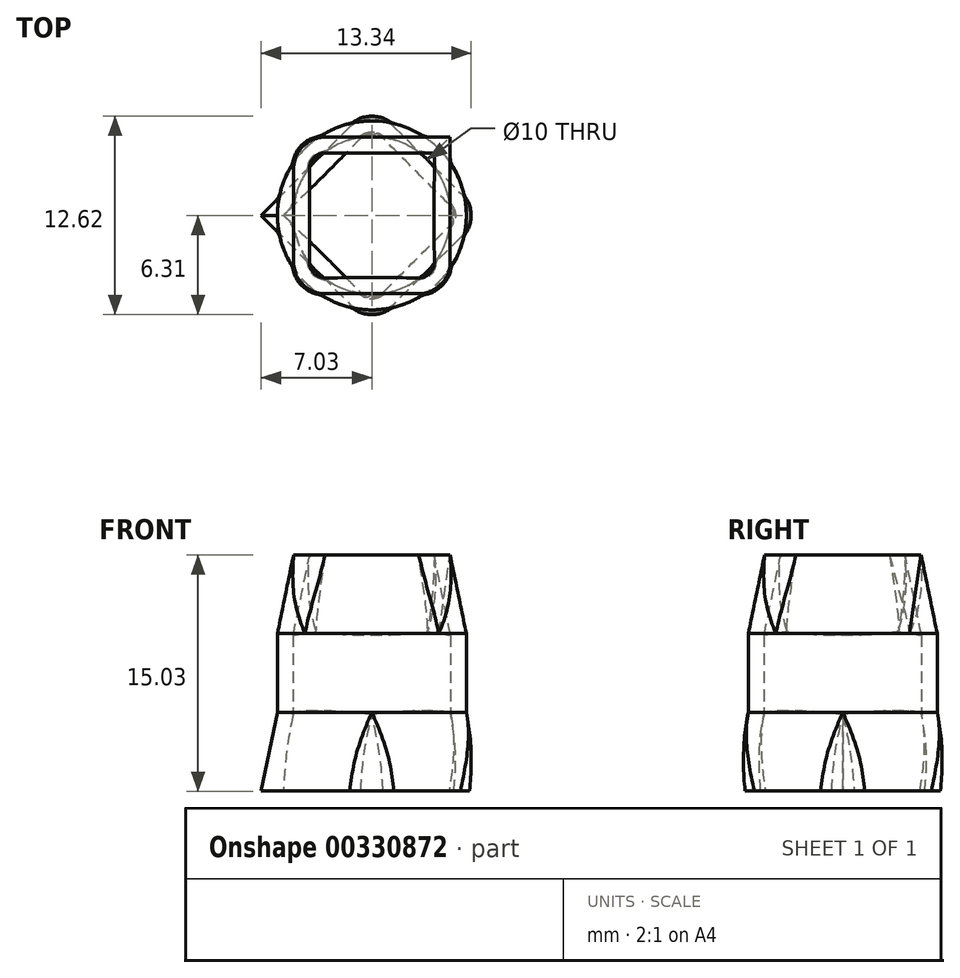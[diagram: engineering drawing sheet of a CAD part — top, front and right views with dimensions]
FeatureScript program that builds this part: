
annotation { "Feature Type Name" : "Feature", "Feature Type Description" : "" }
export const myFeature = defineFeature(function(context is Context, id is Id, definition is map)
    precondition{}
    {
        {
            var Q0;
            Q0=qCreatedBy(makeId("Top.planeOp"),FACE);
            var sketch = newSketch(context, id + "F0", { "sketchPlane" : qUnion([Q0])});
            skCircle(sketch, "E0", {"center": v(0, 0) * mm, "radius": 6 * mm});
            skSolve(sketch);
        }
        {
            var Q0;
            Q0=makeQuery(id+"F0.imprint","IMPRINT",FACE,{"disambiguationData":[TD([[makeQuery(id+"F0.imprint","IMPRINT",EDGE,{"derivedFrom":sQuery(id+"F0.wireOp",EDGE,"E0")}),1.0]])]});
            extrude(context, id + "F1", {"entities" : qUnion([Q0]), "endBound" : BoundingType.SYMMETRIC, "depth" : 5 * mm});
        }
        {
            var Q0;
            Q0=makeQuery(id+"F1.opExtrude","CAP_FACE",FACE,{"disambiguationData":[OSD([sQuery(id+"F0.wireOp",EDGE,"E0")])],"isStart":false});
            cPlane(context, id + "F2", {"entities" : qUnion([Q0]), "cplaneType" : CPlaneType.OFFSET, "offset" : 5 * mm, "width" : 150 * mm, "height" : 150 * mm});
        }
        {
            var Q0;
            Q0=qCreatedBy(id+"F2.planeOp",FACE);
            var sketch = newSketch(context, id + "F3", { "sketchPlane" : qUnion([Q0])});
            skLineSegment(sketch, "E1.bottom", {"start": v(4.97, -4.97) * mm, "end": v(-4.97, -4.97) * mm});
            skLineSegment(sketch, "E1.top", {"start": v(4.97, 4.97) * mm, "end": v(-4.97, 4.97) * mm});
            skLineSegment(sketch, "E1.left", {"start": v(4.97, -4.97) * mm, "end": v(4.97, 4.97) * mm});
            skLineSegment(sketch, "E1.right", {"start": v(-4.97, -4.97) * mm, "end": v(-4.97, 4.97) * mm});
            skPoint(sketch, "E1.middle", {"position": v(0, 0) * mm});
            skLineSegment(sketch, "E2", {"start": v(4.97, 0) * mm, "end": v(6, 0) * mm, "construction": true});
            skPoint(sketch, "E2.endSnap0", {"position": v(4.97, 0) * mm});
            skLineSegment(sketch, "E3", {"start": v(4.97, -4.97) * mm, "end": v(4.24, -4.24) * mm, "construction": true});
            skSolve(sketch);
        }
        {
            var Q0;
            Q0=makeQuery(id+"F1.opExtrude","CAP_FACE",FACE,{"disambiguationData":[OSD([sQuery(id+"F0.wireOp",EDGE,"E0")])],"isStart":false});
            var Q1;
            Q1=makeQuery(id+"F3.imprint","IMPRINT",FACE,{"disambiguationData":[TD([[makeQuery(id+"F3.imprint","IMPRINT",EDGE,{"derivedFrom":sQuery(id+"F3.wireOp",EDGE,"E1.bottom")}),-1.0]])]});
            loft(context, id + "F4", {"operationType" : NewBodyOperationType.ADD, "sheetProfilesArray" : [{ "sheetProfileEntities" : qUnion([Q0]) }, { "sheetProfileEntities" : qUnion([Q1]) }]});
        }
        {
            var Q0;
            Q0=makeQuery(id+"F1.opExtrude","CAP_FACE",FACE,{"disambiguationData":[OSD([sQuery(id+"F0.wireOp",EDGE,"E0")])],"isStart":true});
            cPlane(context, id + "F5", {"entities" : qUnion([Q0]), "cplaneType" : CPlaneType.OFFSET, "offset" : 5 * mm, "width" : 150 * mm, "height" : 150 * mm});
        }
        {
            var Q0;
            Q0=qCreatedBy(id+"F5.planeOp",FACE);
            var sketch = newSketch(context, id + "F6", { "sketchPlane" : qUnion([Q0])});
            skLineSegment(sketch, "E4.bottom", {"start": v(0, -7.03) * mm, "end": v(7.03, 0) * mm});
            skLineSegment(sketch, "E4.top", {"start": v(-7.03, 0) * mm, "end": v(0, 7.03) * mm});
            skLineSegment(sketch, "E4.left", {"start": v(0, -7.03) * mm, "end": v(-7.03, 0) * mm});
            skLineSegment(sketch, "E4.right", {"start": v(7.03, 0) * mm, "end": v(0, 7.03) * mm});
            skPoint(sketch, "E4.middle", {"position": v(0, 0) * mm});
            skSolve(sketch);
        }
        {
            var Q0;
            Q0=makeQuery(id+"F6.imprint","IMPRINT",FACE,{"disambiguationData":[TD([[makeQuery(id+"F6.imprint","IMPRINT",EDGE,{"derivedFrom":sQuery(id+"F6.wireOp",EDGE,"E4.bottom")}),1.0]])]});
            var Q1;
            Q1=makeQuery(id+"F1.opExtrude","CAP_FACE",FACE,{"disambiguationData":[OSD([sQuery(id+"F0.wireOp",EDGE,"E0")])],"isStart":true});
            loft(context, id + "F7", {"operationType" : NewBodyOperationType.ADD, "sheetProfilesArray" : [{ "sheetProfileEntities" : qUnion([Q0]) }, { "sheetProfileEntities" : qUnion([Q1]) }]});
        }
        {
            var Q0;
            Q0=makeQuery(id+"F4.opLoft","SWEPT_EDGE",EDGE,{"disambiguationData":[OSD([sQuery(id+"F0.wireOp",EDGE,"E0"),sQuery(id+"F3.wireOp",EDGE,"E1.top"),sQuery(id+"F3.wireOp",EDGE,"E1.left"),sQuery(id+"F3.wireOp",EDGE,"E1.right")])]});
            var Q1;
            Q1=makeQuery(id+"F4.opLoft","SWEPT_EDGE",EDGE,{"disambiguationData":[OSD([sQuery(id+"F0.wireOp",EDGE,"E0"),sQuery(id+"F3.wireOp",EDGE,"E1.bottom"),sQuery(id+"F3.wireOp",EDGE,"E1.top"),sQuery(id+"F3.wireOp",EDGE,"E1.right")])]});
            var Q2;
            Q2=makeQuery(id+"F4.opLoft","SWEPT_EDGE",EDGE,{"disambiguationData":[OSD([sQuery(id+"F0.wireOp",EDGE,"E0"),sQuery(id+"F3.wireOp",EDGE,"E1.bottom"),sQuery(id+"F3.wireOp",EDGE,"E1.top"),sQuery(id+"F3.wireOp",EDGE,"E1.left")])]});
            var Q3;
            Q3=makeQuery(id+"F4.opLoft","SWEPT_EDGE",EDGE,{"disambiguationData":[OSD([sQuery(id+"F3.wireOp",EDGE,"E1.bottom"),sQuery(id+"F3.wireOp",EDGE,"E1.left")])]});
            var Q4;
            Q4=makeQuery(id+"F7.opLoft","SWEPT_EDGE",EDGE,{"disambiguationData":[OSD([sQuery(id+"F0.wireOp",EDGE,"E0"),sQuery(id+"F6.wireOp",EDGE,"E4.bottom"),sQuery(id+"F6.wireOp",EDGE,"E4.top"),sQuery(id+"F6.wireOp",EDGE,"E4.left")])]});
            var Q5;
            Q5=makeQuery(id+"F7.opLoft","SWEPT_EDGE",EDGE,{"disambiguationData":[OSD([sQuery(id+"F0.wireOp",EDGE,"E0"),sQuery(id+"F6.wireOp",EDGE,"E4.top"),sQuery(id+"F6.wireOp",EDGE,"E4.left"),sQuery(id+"F6.wireOp",EDGE,"E4.right")])]});
            var Q6;
            Q6=makeQuery(id+"F7.opLoft","SWEPT_EDGE",EDGE,{"disambiguationData":[OSD([sQuery(id+"F6.wireOp",EDGE,"E4.bottom"),sQuery(id+"F6.wireOp",EDGE,"E4.left")])]});
            var Q7;
            Q7=makeQuery(id+"F7.opLoft","SWEPT_EDGE",EDGE,{"disambiguationData":[OSD([sQuery(id+"F0.wireOp",EDGE,"E0"),sQuery(id+"F6.wireOp",EDGE,"E4.bottom"),sQuery(id+"F6.wireOp",EDGE,"E4.top"),sQuery(id+"F6.wireOp",EDGE,"E4.right")])]});
            fillet(context, id + "F8", {"entities" : qUnion([Q0, Q1, Q2, Q3, Q4, Q5, Q6, Q7]), "radius" : 2 * mm, "tangentPropagation" : true, "allowEdgeOverflow" : false});
        }
        {
            var Q0;
            Q0=makeQuery(id+"F7.opLoft","CAP_FACE",FACE,{"disambiguationData":[OSD([makeQuery(id+"F6.imprint","IMPRINT",FACE,{"disambiguationData":[TD([[makeQuery(id+"F6.imprint","IMPRINT",EDGE,{"derivedFrom":sQuery(id+"F6.wireOp",EDGE,"E4.bottom")}),1.0]])]})])],"isStart":true});
            var Q1;
            Q1=makeQuery(id+"F4.opLoft","CAP_FACE",FACE,{"disambiguationData":[OSD([makeQuery(id+"F3.imprint","IMPRINT",FACE,{"disambiguationData":[TD([[makeQuery(id+"F3.imprint","IMPRINT",EDGE,{"derivedFrom":sQuery(id+"F3.wireOp",EDGE,"E1.bottom")}),-1.0]])]})])],"isStart":true});
            shell(context, id + "F9", {"entities" : qUnion([Q0, Q1]), "thickness" : 1 * mm});
        }
    });
